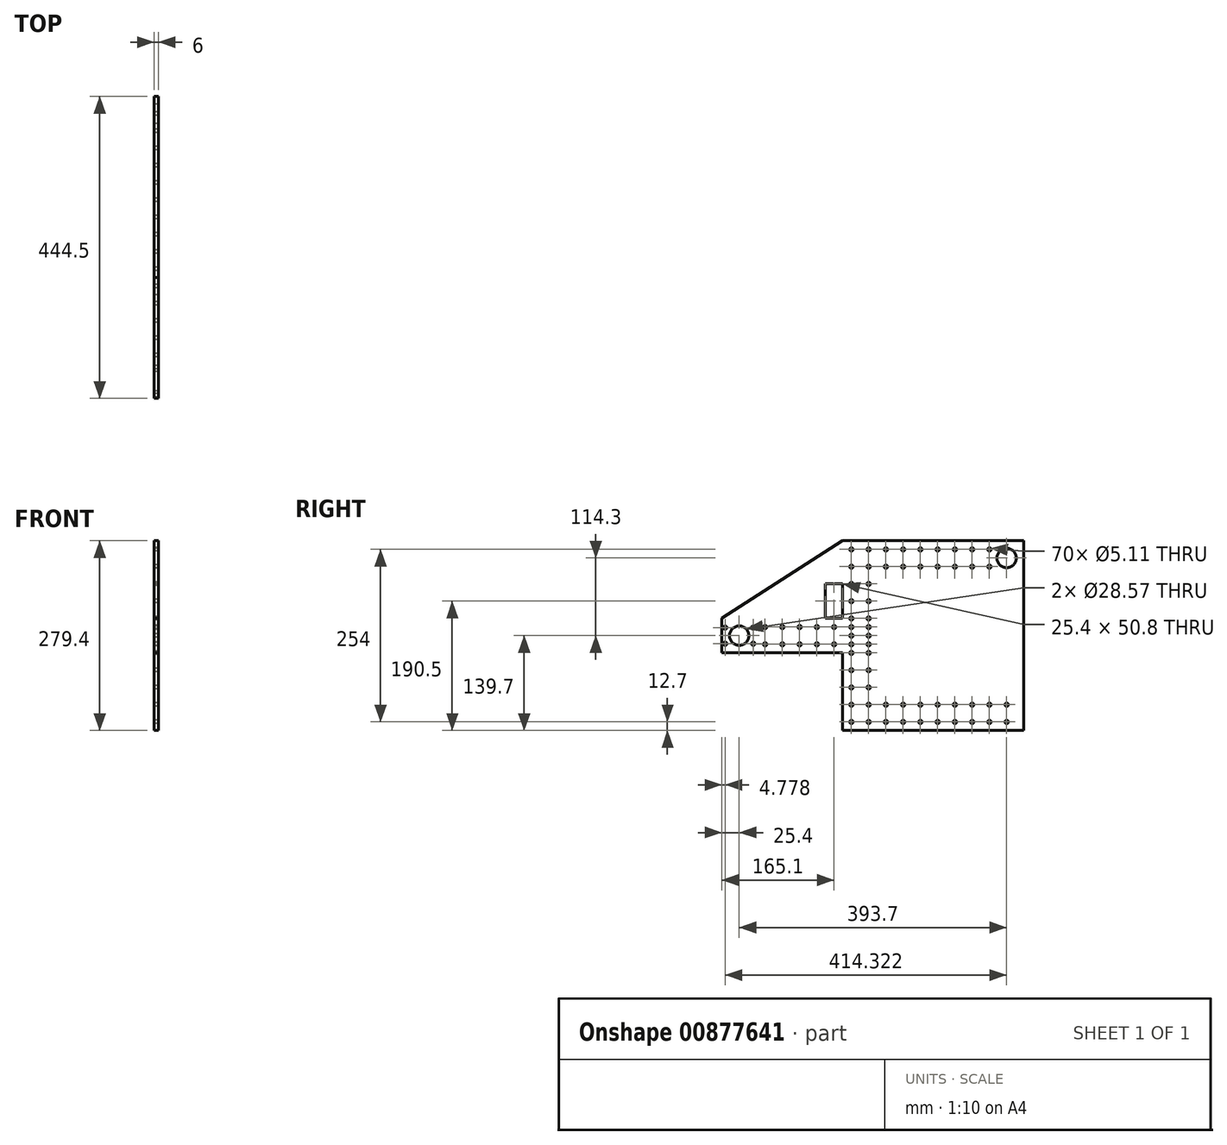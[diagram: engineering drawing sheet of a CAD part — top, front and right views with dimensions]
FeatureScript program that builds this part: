
annotation { "Feature Type Name" : "Feature", "Feature Type Description" : "" }
export const myFeature = defineFeature(function(context is Context, id is Id, definition is map)
    precondition{}
    {
        {
            var Q0;
            Q0=qCreatedBy(makeId("Right.planeOp"),FACE);
            var sketch = newSketch(context, id + "F0", { "sketchPlane" : qUnion([Q0])});
            skLineSegment(sketch, "E0.bottom", {"start": v(0, 25.4) * mm, "end": v(177.8, 25.4) * mm, "construction": true});
            skLineSegment(sketch, "E0.top", {"start": v(0, -25.4) * mm, "end": v(177.8, -25.4) * mm, "construction": true});
            skLineSegment(sketch, "E0.left", {"start": v(0, 25.4) * mm, "end": v(0, -25.4) * mm});
            skLineSegment(sketch, "E0.right", {"start": v(177.8, 25.4) * mm, "end": v(177.8, -25.4) * mm, "construction": true});
            skPoint(sketch, "E0.middle", {"position": v(88.9, 0) * mm});
            skLineSegment(sketch, "E1.bottom", {"start": v(177.8, 139.7) * mm, "end": v(228.6, 139.7) * mm, "construction": true});
            skLineSegment(sketch, "E1.top", {"start": v(177.8, -139.7) * mm, "end": v(228.6, -139.7) * mm, "construction": true});
            skLineSegment(sketch, "E1.left", {"start": v(177.8, 139.7) * mm, "end": v(177.8, -139.7) * mm, "construction": true});
            skLineSegment(sketch, "E1.right", {"start": v(228.6, 139.7) * mm, "end": v(228.6, -139.7) * mm, "construction": true});
            skPoint(sketch, "E1.middle", {"position": v(203.2, 0) * mm});
            skLineSegment(sketch, "E2.bottom", {"start": v(228.6, -139.7) * mm, "end": v(444.5, -139.7) * mm, "construction": true});
            skLineSegment(sketch, "E2.top", {"start": v(228.6, -88.9) * mm, "end": v(444.5, -88.9) * mm, "construction": true});
            skLineSegment(sketch, "E2.left", {"start": v(228.6, -139.7) * mm, "end": v(228.6, -88.9) * mm, "construction": true});
            skLineSegment(sketch, "E2.right", {"start": v(444.5, -139.7) * mm, "end": v(444.5, -88.9) * mm, "construction": true});
            skLineSegment(sketch, "E3.bottom", {"start": v(228.6, 139.7) * mm, "end": v(444.5, 139.7) * mm, "construction": true});
            skLineSegment(sketch, "E3.top", {"start": v(228.6, 88.9) * mm, "end": v(444.5, 88.9) * mm, "construction": true});
            skLineSegment(sketch, "E3.left", {"start": v(228.6, 139.7) * mm, "end": v(228.6, 88.9) * mm, "construction": true});
            skLineSegment(sketch, "E3.right", {"start": v(444.5, 139.7) * mm, "end": v(444.5, 88.9) * mm, "construction": true});
            skCircle(sketch, "E4", {"center": v(419.1, 114.3) * mm, "radius": 14.29 * mm});
            skLineSegment(sketch, "E5", {"start": v(0, 25.4) * mm, "end": v(177.8, 139.7) * mm});
            skLineSegment(sketch, "E6", {"start": v(177.8, 139.7) * mm, "end": v(444.5, 139.7) * mm});
            skLineSegment(sketch, "E7", {"start": v(444.5, 139.7) * mm, "end": v(444.5, -139.7) * mm});
            skLineSegment(sketch, "E8", {"start": v(444.5, -139.7) * mm, "end": v(177.8, -139.7) * mm});
            skLineSegment(sketch, "E9", {"start": v(177.8, -139.7) * mm, "end": v(177.8, -25.4) * mm});
            skLineSegment(sketch, "E10", {"start": v(177.8, -25.4) * mm, "end": v(0, -25.4) * mm});
            skCircle(sketch, "E11", {"center": v(25.4, 0) * mm, "radius": 14.29 * mm});
            skLineSegment(sketch, "E12", {"start": v(25.4, 0) * mm, "end": v(25.4, 23.81) * mm, "construction": true});
            skCircle(sketch, "E13", {"center": v(25.4, 23.81) * mm, "radius": 2.55 * mm, "construction": true});
            skLineSegment(sketch, "E14.1.0", {"start": v(25.4, 0) * mm, "end": v(4.78, 11.9) * mm, "construction": true});
            skCircle(sketch, "E14.1.1", {"center": v(4.78, 11.9) * mm, "radius": 2.55 * mm});
            skLineSegment(sketch, "E14.2.0", {"start": v(25.4, 0) * mm, "end": v(4.78, -11.9) * mm, "construction": true});
            skCircle(sketch, "E14.2.1", {"center": v(4.78, -11.9) * mm, "radius": 2.55 * mm});
            skLineSegment(sketch, "E14.3.0", {"start": v(25.4, 0) * mm, "end": v(25.4, -23.81) * mm, "construction": true});
            skCircle(sketch, "E14.3.1", {"center": v(25.4, -23.81) * mm, "radius": 2.55 * mm, "construction": true});
            skLineSegment(sketch, "E14.4.0", {"start": v(25.4, 0) * mm, "end": v(46.02, -11.9) * mm, "construction": true});
            skCircle(sketch, "E14.4.1", {"center": v(46.02, -11.9) * mm, "radius": 2.55 * mm});
            skLineSegment(sketch, "E14.5.0", {"start": v(25.4, 0) * mm, "end": v(46.02, 11.9) * mm, "construction": true});
            skCircle(sketch, "E14.5.1", {"center": v(46.02, 11.9) * mm, "radius": 2.55 * mm});
            skCircle(sketch, "E15", {"center": v(63.5, 12.7) * mm, "radius": 2.55 * mm});
            skCircle(sketch, "E16.0.1.0", {"center": v(63.5, -12.7) * mm, "radius": 2.55 * mm});
            skCircle(sketch, "E16.1.0.0", {"center": v(88.9, 12.7) * mm, "radius": 2.55 * mm});
            skCircle(sketch, "E16.1.1.0", {"center": v(88.9, -12.7) * mm, "radius": 2.55 * mm});
            skCircle(sketch, "E16.2.0.0", {"center": v(114.3, 12.7) * mm, "radius": 2.55 * mm});
            skCircle(sketch, "E16.2.1.0", {"center": v(114.3, -12.7) * mm, "radius": 2.55 * mm});
            skCircle(sketch, "E16.3.0.0", {"center": v(139.7, 12.7) * mm, "radius": 2.55 * mm});
            skCircle(sketch, "E16.3.1.0", {"center": v(139.7, -12.7) * mm, "radius": 2.55 * mm});
            skCircle(sketch, "E16.4.0.0", {"center": v(165.1, 12.7) * mm, "radius": 2.55 * mm});
            skCircle(sketch, "E16.4.1.0", {"center": v(165.1, -12.7) * mm, "radius": 2.55 * mm});
            skCircle(sketch, "E16.5.0.0", {"center": v(190.5, 12.7) * mm, "radius": 2.55 * mm});
            skCircle(sketch, "E16.5.1.0", {"center": v(190.5, -12.7) * mm, "radius": 2.55 * mm});
            skCircle(sketch, "E16.6.0.0", {"center": v(215.9, 12.7) * mm, "radius": 2.55 * mm});
            skCircle(sketch, "E16.6.1.0", {"center": v(215.9, -12.7) * mm, "radius": 2.55 * mm});
            skLineSegment(sketch, "E16.direction1", {"start": v(63.5, 12.7) * mm, "end": v(88.9, 12.7) * mm, "construction": true});
            skLineSegment(sketch, "E16.direction2", {"start": v(63.5, 12.7) * mm, "end": v(63.5, -12.7) * mm, "construction": true});
            skCircle(sketch, "E17", {"center": v(190.5, 127) * mm, "radius": 2.55 * mm});
            skCircle(sketch, "E18.0.1.0", {"center": v(190.5, 101.6) * mm, "radius": 2.55 * mm});
            skCircle(sketch, "E18.0.2.0", {"center": v(190.5, 76.2) * mm, "radius": 2.55 * mm});
            skCircle(sketch, "E18.0.3.0", {"center": v(190.5, 50.8) * mm, "radius": 2.55 * mm});
            skCircle(sketch, "E18.0.4.0", {"center": v(190.5, 25.4) * mm, "radius": 2.55 * mm});
            skCircle(sketch, "E18.0.5.0", {"center": v(190.5, 0) * mm, "radius": 2.55 * mm});
            skCircle(sketch, "E18.0.6.0", {"center": v(190.5, -25.4) * mm, "radius": 2.55 * mm});
            skCircle(sketch, "E18.0.7.0", {"center": v(190.5, -50.8) * mm, "radius": 2.55 * mm});
            skCircle(sketch, "E18.0.8.0", {"center": v(190.5, -76.2) * mm, "radius": 2.55 * mm});
            skCircle(sketch, "E18.0.9.0", {"center": v(190.5, -101.6) * mm, "radius": 2.55 * mm});
            skCircle(sketch, "E18.0.10.0", {"center": v(190.5, -127) * mm, "radius": 2.55 * mm});
            skCircle(sketch, "E18.1.0.0", {"center": v(215.9, 127) * mm, "radius": 2.55 * mm});
            skCircle(sketch, "E18.1.1.0", {"center": v(215.9, 101.6) * mm, "radius": 2.55 * mm});
            skCircle(sketch, "E18.1.2.0", {"center": v(215.9, 76.2) * mm, "radius": 2.55 * mm});
            skCircle(sketch, "E18.1.3.0", {"center": v(215.9, 50.8) * mm, "radius": 2.55 * mm});
            skCircle(sketch, "E18.1.4.0", {"center": v(215.9, 25.4) * mm, "radius": 2.55 * mm});
            skCircle(sketch, "E18.1.5.0", {"center": v(215.9, 0) * mm, "radius": 2.55 * mm});
            skCircle(sketch, "E18.1.6.0", {"center": v(215.9, -25.4) * mm, "radius": 2.55 * mm});
            skCircle(sketch, "E18.1.7.0", {"center": v(215.9, -50.8) * mm, "radius": 2.55 * mm});
            skCircle(sketch, "E18.1.8.0", {"center": v(215.9, -76.2) * mm, "radius": 2.55 * mm});
            skCircle(sketch, "E18.1.9.0", {"center": v(215.9, -101.6) * mm, "radius": 2.55 * mm});
            skCircle(sketch, "E18.1.10.0", {"center": v(215.9, -127) * mm, "radius": 2.55 * mm});
            skLineSegment(sketch, "E18.direction1", {"start": v(190.5, 127) * mm, "end": v(215.9, 127) * mm, "construction": true});
            skLineSegment(sketch, "E18.direction2", {"start": v(190.5, 127) * mm, "end": v(190.5, 101.6) * mm, "construction": true});
            skCircle(sketch, "E19", {"center": v(241.3, -127) * mm, "radius": 2.55 * mm});
            skCircle(sketch, "E20.0.1.0", {"center": v(241.3, -101.6) * mm, "radius": 2.55 * mm});
            skCircle(sketch, "E20.1.0.0", {"center": v(266.7, -127) * mm, "radius": 2.55 * mm});
            skCircle(sketch, "E20.1.1.0", {"center": v(266.7, -101.6) * mm, "radius": 2.55 * mm});
            skCircle(sketch, "E20.2.0.0", {"center": v(292.1, -127) * mm, "radius": 2.55 * mm});
            skCircle(sketch, "E20.2.1.0", {"center": v(292.1, -101.6) * mm, "radius": 2.55 * mm});
            skCircle(sketch, "E20.3.0.0", {"center": v(317.5, -127) * mm, "radius": 2.55 * mm});
            skCircle(sketch, "E20.3.1.0", {"center": v(317.5, -101.6) * mm, "radius": 2.55 * mm});
            skCircle(sketch, "E20.4.0.0", {"center": v(342.9, -127) * mm, "radius": 2.55 * mm});
            skCircle(sketch, "E20.4.1.0", {"center": v(342.9, -101.6) * mm, "radius": 2.55 * mm});
            skCircle(sketch, "E20.5.0.0", {"center": v(368.3, -127) * mm, "radius": 2.55 * mm});
            skCircle(sketch, "E20.5.1.0", {"center": v(368.3, -101.6) * mm, "radius": 2.55 * mm});
            skLineSegment(sketch, "E20.direction1", {"start": v(241.3, -127) * mm, "end": v(266.7, -127) * mm, "construction": true});
            skLineSegment(sketch, "E20.direction2", {"start": v(241.3, -127) * mm, "end": v(241.3, -101.6) * mm, "construction": true});
            skLineSegment(sketch, "E21", {"start": v(228.6, 0) * mm, "end": v(203.2, 0) * mm, "construction": true});
            skCircle(sketch, "E22.MirrorC", {"center": v(241.3, 127) * mm, "radius": 2.55 * mm});
            skCircle(sketch, "E23.MirrorC", {"center": v(241.3, 101.6) * mm, "radius": 2.55 * mm});
            skCircle(sketch, "E24.MirrorC", {"center": v(266.7, 127) * mm, "radius": 2.55 * mm});
            skCircle(sketch, "E25.MirrorC", {"center": v(292.1, 101.6) * mm, "radius": 2.55 * mm});
            skCircle(sketch, "E26.MirrorC", {"center": v(292.1, 127) * mm, "radius": 2.55 * mm});
            skCircle(sketch, "E27.MirrorC", {"center": v(317.5, 101.6) * mm, "radius": 2.55 * mm});
            skCircle(sketch, "E28.MirrorC", {"center": v(266.7, 101.6) * mm, "radius": 2.55 * mm});
            skCircle(sketch, "E29.MirrorC", {"center": v(317.5, 127) * mm, "radius": 2.55 * mm});
            skLineSegment(sketch, "E30.MirrorCS", {"start": v(241.3, 127) * mm, "end": v(241.3, 101.6) * mm, "construction": true});
            skLineSegment(sketch, "E31.MirrorCS", {"start": v(241.3, 127) * mm, "end": v(266.7, 127) * mm, "construction": true});
            skCircle(sketch, "E32.MirrorC", {"center": v(342.9, 127) * mm, "radius": 2.55 * mm});
            skCircle(sketch, "E33.MirrorC", {"center": v(342.9, 101.6) * mm, "radius": 2.55 * mm});
            skCircle(sketch, "E34.0.6.0", {"center": v(393.7, -127) * mm, "radius": 2.55 * mm});
            skCircle(sketch, "E34.0.6.1", {"center": v(393.7, -101.6) * mm, "radius": 2.55 * mm});
            skCircle(sketch, "E34.0.7.0", {"center": v(419.1, -127) * mm, "radius": 2.55 * mm});
            skCircle(sketch, "E34.0.7.1", {"center": v(419.1, -101.6) * mm, "radius": 2.55 * mm});
            skCircle(sketch, "E35.MirrorC", {"center": v(393.7, 101.6) * mm, "radius": 2.55 * mm});
            skCircle(sketch, "E36.MirrorC", {"center": v(393.7, 127) * mm, "radius": 2.55 * mm});
            skCircle(sketch, "E37.MirrorC", {"center": v(368.3, 127) * mm, "radius": 2.55 * mm});
            skCircle(sketch, "E38.MirrorC", {"center": v(368.3, 101.6) * mm, "radius": 2.55 * mm});
            skLineSegment(sketch, "E39.bottom", {"start": v(177.8, 25.4) * mm, "end": v(152.4, 25.4) * mm});
            skLineSegment(sketch, "E39.top", {"start": v(177.8, 76.2) * mm, "end": v(152.4, 76.2) * mm});
            skLineSegment(sketch, "E39.left", {"start": v(177.8, 25.4) * mm, "end": v(177.8, 76.2) * mm});
            skLineSegment(sketch, "E39.right", {"start": v(152.4, 25.4) * mm, "end": v(152.4, 76.2) * mm});
            skSolve(sketch);
        }
        {
            var Q0;
            Q0=makeQuery(id+"F0.imprint","IMPRINT",FACE,{"disambiguationData":[TD([[makeQuery(id+"F0.imprint","IMPRINT",EDGE,{"derivedFrom":sQuery(id+"F0.wireOp",EDGE,"E0.left")}),1.0]])]});
            extrude(context, id + "F1", {"entities" : qUnion([Q0]), "depth" : 6 * mm, "offsetDistance" : 25.4 * mm});
        }
    });
